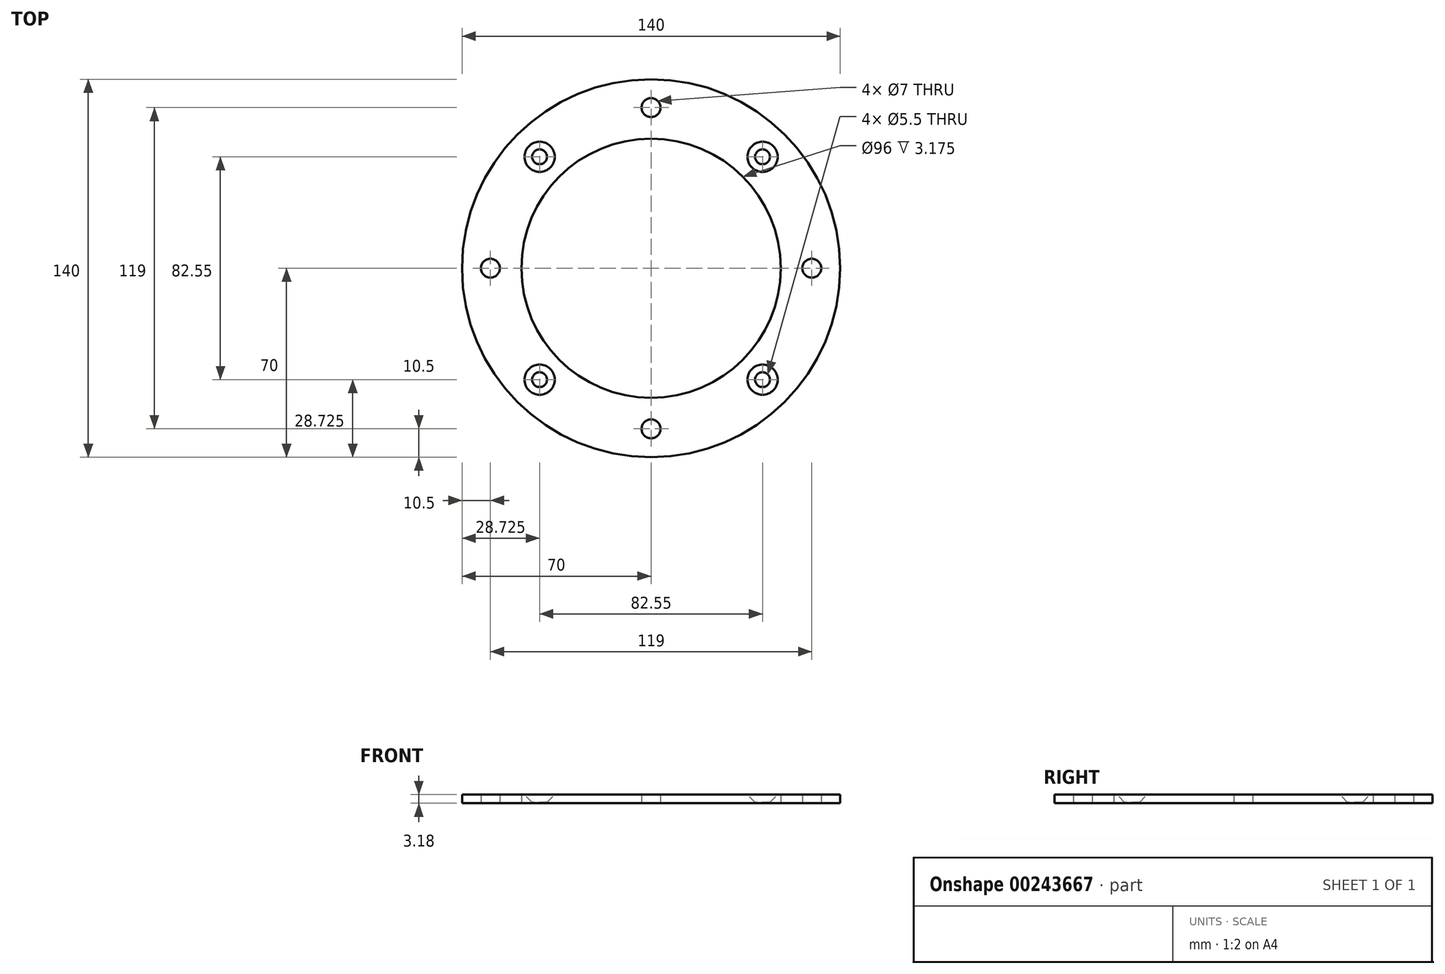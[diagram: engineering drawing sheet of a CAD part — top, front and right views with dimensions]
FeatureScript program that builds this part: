
annotation { "Feature Type Name" : "Feature", "Feature Type Description" : "" }
export const myFeature = defineFeature(function(context is Context, id is Id, definition is map)
    precondition{}
    {
        {
            var Q0;
            Q0=qCreatedBy(makeId("Top.planeOp"),FACE);
            var sketch = newSketch(context, id + "F0", { "sketchPlane" : qUnion([Q0])});
            skCircle(sketch, "E0", {"center": v(0, 0) * mm, "radius": 70 * mm});
            skLineSegment(sketch, "E1", {"start": v(0, 0) * mm, "end": v(0, 59.5) * mm, "construction": true});
            skLineSegment(sketch, "E2", {"start": v(0, 0) * mm, "end": v(59.5, 0) * mm, "construction": true});
            skLineSegment(sketch, "E3", {"start": v(0, 0) * mm, "end": v(-59.5, 0) * mm, "construction": true});
            skLineSegment(sketch, "E4", {"start": v(0, 0) * mm, "end": v(0, -59.5) * mm, "construction": true});
            skCircle(sketch, "E5", {"center": v(0, 59.5) * mm, "radius": 3.5 * mm});
            skCircle(sketch, "E6", {"center": v(59.5, 0) * mm, "radius": 3.5 * mm});
            skCircle(sketch, "E7", {"center": v(0, -59.5) * mm, "radius": 3.5 * mm});
            skCircle(sketch, "E8", {"center": v(-59.5, 0) * mm, "radius": 3.5 * mm});
            skCircle(sketch, "E9", {"center": v(0, 0) * mm, "radius": 48 * mm});
            skSolve(sketch);
        }
        {
            var Q0;
            Q0 = qSketchRegion(id + "F0", true);
            extrude(context, id + "F1", {"entities" : qUnion([Q0]), "endBound" : BoundingType.SYMMETRIC, "depth" : 3.17 * mm});
        }
        {
            var Q0;
            Q0=makeQuery(id+"F1.opExtrude","CAP_FACE",FACE,{"disambiguationData":[OSD([sQuery(id+"F0.wireOp",EDGE,"E0"),sQuery(id+"F0.wireOp",EDGE,"E5"),sQuery(id+"F0.wireOp",EDGE,"E6"),sQuery(id+"F0.wireOp",EDGE,"E7"),sQuery(id+"F0.wireOp",EDGE,"E8"),sQuery(id+"F0.wireOp",EDGE,"E9")])],"isStart":false});
            var sketch = newSketch(context, id + "F2", { "sketchPlane" : qUnion([Q0])});
            skLineSegment(sketch, "E10.bottom", {"start": v(-52.55, -52.55) * mm, "end": v(52.55, -52.55) * mm, "construction": true});
            skLineSegment(sketch, "E10.top", {"start": v(-52.55, 52.55) * mm, "end": v(52.55, 52.55) * mm, "construction": true});
            skLineSegment(sketch, "E10.left", {"start": v(-52.55, -52.55) * mm, "end": v(-52.55, 52.55) * mm, "construction": true});
            skLineSegment(sketch, "E10.right", {"start": v(52.55, -52.55) * mm, "end": v(52.55, 52.55) * mm, "construction": true});
            skPoint(sketch, "E10.middle", {"position": v(0, 0) * mm});
            skLineSegment(sketch, "E11.bottom", {"start": v(-41.28, -41.28) * mm, "end": v(41.28, -41.28) * mm, "construction": true});
            skLineSegment(sketch, "E11.top", {"start": v(-41.27, 41.28) * mm, "end": v(41.28, 41.28) * mm, "construction": true});
            skLineSegment(sketch, "E11.left", {"start": v(-41.28, -41.28) * mm, "end": v(-41.27, 41.28) * mm, "construction": true});
            skLineSegment(sketch, "E11.right", {"start": v(41.28, -41.28) * mm, "end": v(41.28, 41.28) * mm, "construction": true});
            skSolve(sketch);
        }
        {
            var Q0;
            Q0=sQuery(id+"F2.wireOp",VERTEX,"E11.left.end");
            var Q1;
            Q1=sQuery(id+"F2.wireOp",VERTEX,"E11.right.end");
            var Q2;
            Q2=sQuery(id+"F2.wireOp",VERTEX,"E11.right.start");
            var Q3;
            Q3=sQuery(id+"F2.wireOp",VERTEX,"E11.left.start");
            var Q4;
            Q4=makeQuery(id+"F1.opExtrude","SWEPT_BODY",BODY,{"disambiguationData":[OSD([sQuery(id+"F0.wireOp",EDGE,"E0"),sQuery(id+"F0.wireOp",EDGE,"E5"),sQuery(id+"F0.wireOp",EDGE,"E6"),sQuery(id+"F0.wireOp",EDGE,"E7"),sQuery(id+"F0.wireOp",EDGE,"E8"),sQuery(id+"F0.wireOp",EDGE,"E9")])]});
            hole(context, id + "F3", {"style" : HoleStyle.C_SINK, "endStyle" : HoleEndStyle.BLIND, "standardTappedOrClearance" : lookupTablePath({ "standard" : "ISO", "fit" : "Normal", "size" : "M5", "type" : "Clearance" }), "standardBlindInLast" : lookupTablePath({ "fit" : "Standard", "standard" : "ISO", "size" : "M5", "type" : "Clearance" }), "holeDiameter" : 5.5 * mm, "cSinkDiameter" : 11.2 * mm, "cSinkAngle" : 90 * degree, "holeDepth" : 15 * mm, "tappedDepth" : 12.7 * mm, "tapClearance" : 3, "locations" : qUnion([Q0, Q1, Q2, Q3]), "scope" : qUnion([Q4])});
        }
    });
